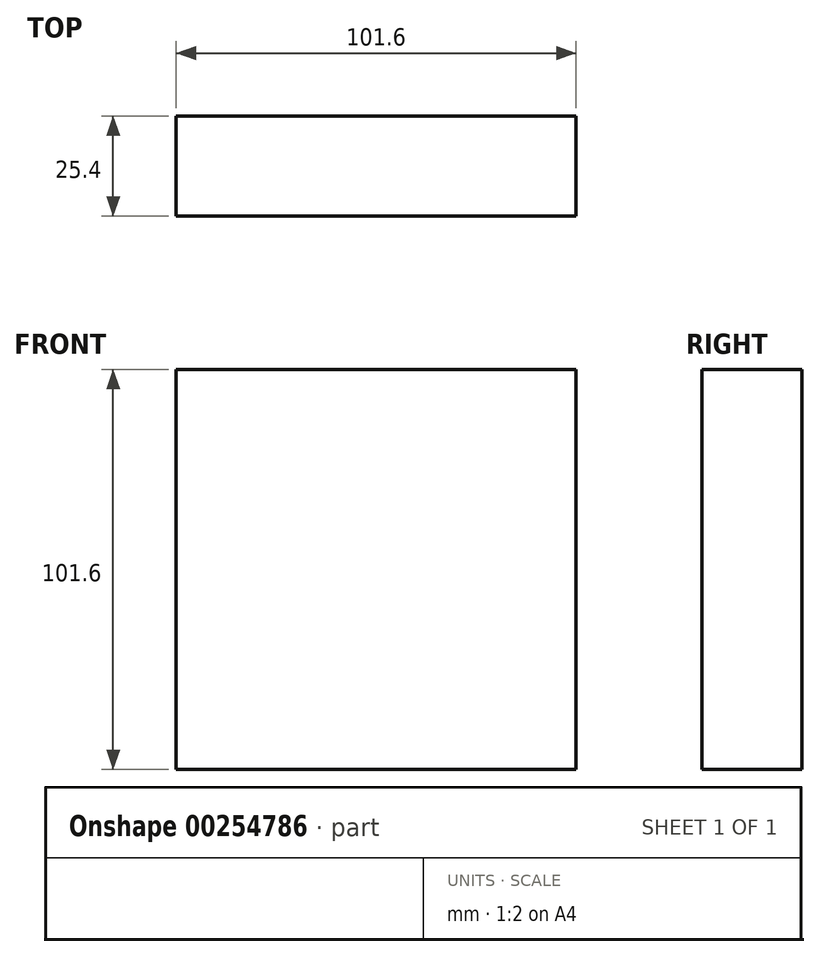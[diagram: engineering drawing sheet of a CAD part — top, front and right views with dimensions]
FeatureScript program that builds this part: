
annotation { "Feature Type Name" : "Feature", "Feature Type Description" : "" }
export const myFeature = defineFeature(function(context is Context, id is Id, definition is map)
    precondition{}
    {
        {
            var Q0;
            Q0=qCreatedBy(makeId("Front.planeOp"),FACE);
            var sketch = newSketch(context, id + "F0", { "sketchPlane" : qUnion([Q0])});
            skLineSegment(sketch, "E0.bottom", {"start": v(52.4, -50.8) * mm, "end": v(-49.2, -50.8) * mm});
            skLineSegment(sketch, "E0.top", {"start": v(52.4, 50.8) * mm, "end": v(-49.2, 50.8) * mm});
            skLineSegment(sketch, "E0.left", {"start": v(52.4, -50.8) * mm, "end": v(52.4, 50.8) * mm});
            skLineSegment(sketch, "E0.right", {"start": v(-49.2, -50.8) * mm, "end": v(-49.2, 50.8) * mm});
            skPoint(sketch, "E0.middle", {"position": v(1.6, 0) * mm});
            skSolve(sketch);
        }
        {
            var Q0;
            Q0=makeQuery(id+"F0.imprint","IMPRINT",FACE,{"disambiguationData":[TD([[makeQuery(id+"F0.imprint","IMPRINT",EDGE,{"derivedFrom":sQuery(id+"F0.wireOp",EDGE,"E0.bottom")}),-1.0]])]});
            extrude(context, id + "F1", {"entities" : qUnion([Q0]), "depth" : 25.4 * mm});
        }
    });
